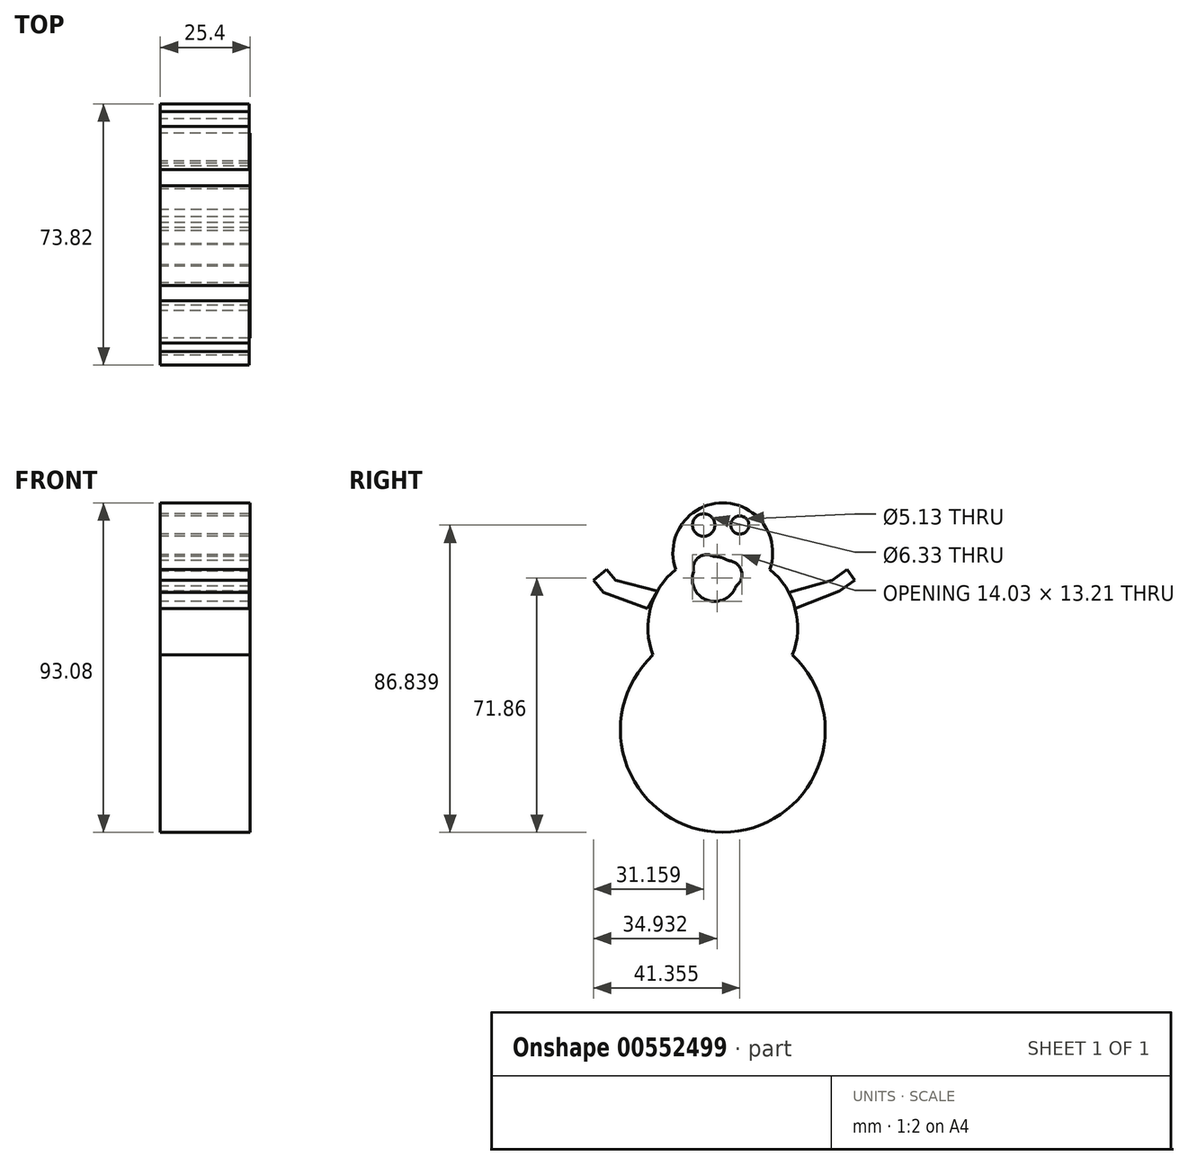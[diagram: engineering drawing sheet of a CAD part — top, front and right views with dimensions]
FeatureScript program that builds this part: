
annotation { "Feature Type Name" : "Feature", "Feature Type Description" : "" }
export const myFeature = defineFeature(function(context is Context, id is Id, definition is map)
    precondition{}
    {
        {
            var Q0;
            Q0=qCreatedBy(makeId("Right.planeOp"),FACE);
            var sketch = newSketch(context, id + "F0", { "sketchPlane" : qUnion([Q0])});
            skCircle(sketch, "E0", {"center": v(0, 0) * mm, "radius": 28.92 * mm});
            skCircle(sketch, "E1", {"center": v(0, 28.92) * mm, "radius": 21.15 * mm});
            skCircle(sketch, "E2", {"center": v(0, 50.07) * mm, "radius": 14.1 * mm});
            skCircle(sketch, "E3", {"center": v(4.81, 57.92) * mm, "radius": 2.56 * mm});
            skCircle(sketch, "E4", {"center": v(-5.38, 57.92) * mm, "radius": 3.17 * mm});
            skCircle(sketch, "E5", {"center": v(-4.53, 45.74) * mm, "radius": 2.27 * mm});
            skCircle(sketch, "E6", {"center": v(-4.53, 45.74) * mm, "radius": 3.81 * mm});
            skCircle(sketch, "E7", {"center": v(-0.72, 45.74) * mm, "radius": 2.86 * mm});
            skCircle(sketch, "E8", {"center": v(2.13, 45.74) * mm, "radius": 1.96 * mm});
            skCircle(sketch, "E9", {"center": v(1.46, 43.9) * mm, "radius": 3.94 * mm});
            skCircle(sketch, "E10", {"center": v(-2.29, 42.66) * mm, "radius": 6.34 * mm});
            skSolve(sketch);
        }
        {
            var Q0;
            Q0 = qSketchRegion(id + "F0", true);
            extrude(context, id + "F1", {"entities" : qUnion([Q0]), "depth" : 25.4 * mm, "offsetDistance" : 25.4 * mm});
        }
        {
            var Q0;
            Q0=makeQuery(id+"F1.opExtrude","CAP_FACE",FACE,{"disambiguationData":[OSD([sQuery(id+"F0.wireOp",EDGE,"E0"),sQuery(id+"F0.wireOp",EDGE,"E1"),sQuery(id+"F0.wireOp",EDGE,"E2"),sQuery(id+"F0.wireOp",EDGE,"E3"),sQuery(id+"F0.wireOp",EDGE,"E4"),sQuery(id+"F0.wireOp",EDGE,"E6"),sQuery(id+"F0.wireOp",EDGE,"E9"),sQuery(id+"F0.wireOp",EDGE,"E10")])],"isStart":true});
            var sketch = newSketch(context, id + "F2", { "sketchPlane" : qUnion([Q0])});
            skLineSegment(sketch, "E11", {"start": v(-18.68, 38.84) * mm, "end": v(-30.87, 42.34) * mm});
            skLineSegment(sketch, "E12", {"start": v(-30.87, 42.34) * mm, "end": v(-35.12, 45.37) * mm});
            skLineSegment(sketch, "E13", {"start": v(-35.12, 45.37) * mm, "end": v(-37.28, 42.34) * mm});
            skLineSegment(sketch, "E14", {"start": v(-37.28, 42.34) * mm, "end": v(-32.98, 39.27) * mm});
            skLineSegment(sketch, "E15", {"start": v(-32.98, 39.27) * mm, "end": v(-20.45, 34.33) * mm});
            skLineSegment(sketch, "E16", {"start": v(-20.45, 34.33) * mm, "end": v(-18.68, 38.84) * mm});
            skLineSegment(sketch, "E17", {"start": v(18.44, 39.27) * mm, "end": v(21.22, 34.33) * mm});
            skLineSegment(sketch, "E18", {"start": v(21.22, 34.33) * mm, "end": v(33.7, 38.84) * mm});
            skLineSegment(sketch, "E19", {"start": v(33.7, 38.84) * mm, "end": v(36.54, 42.34) * mm});
            skLineSegment(sketch, "E20", {"start": v(36.54, 42.34) * mm, "end": v(32.8, 45.37) * mm});
            skLineSegment(sketch, "E21", {"start": v(32.8, 45.37) * mm, "end": v(30.34, 42.34) * mm});
            skLineSegment(sketch, "E22", {"start": v(30.34, 42.34) * mm, "end": v(18.44, 39.27) * mm});
            skSolve(sketch);
        }
        {
            var Q0;
            Q0 = qSketchRegion(id + "F2", true);
            extrude(context, id + "F3", {"entities" : qUnion([Q0]), "operationType" : NewBodyOperationType.ADD, "oppositeDirection" : true, "depth" : 25.15 * mm, "offsetDistance" : 25.4 * mm});
        }
    });
